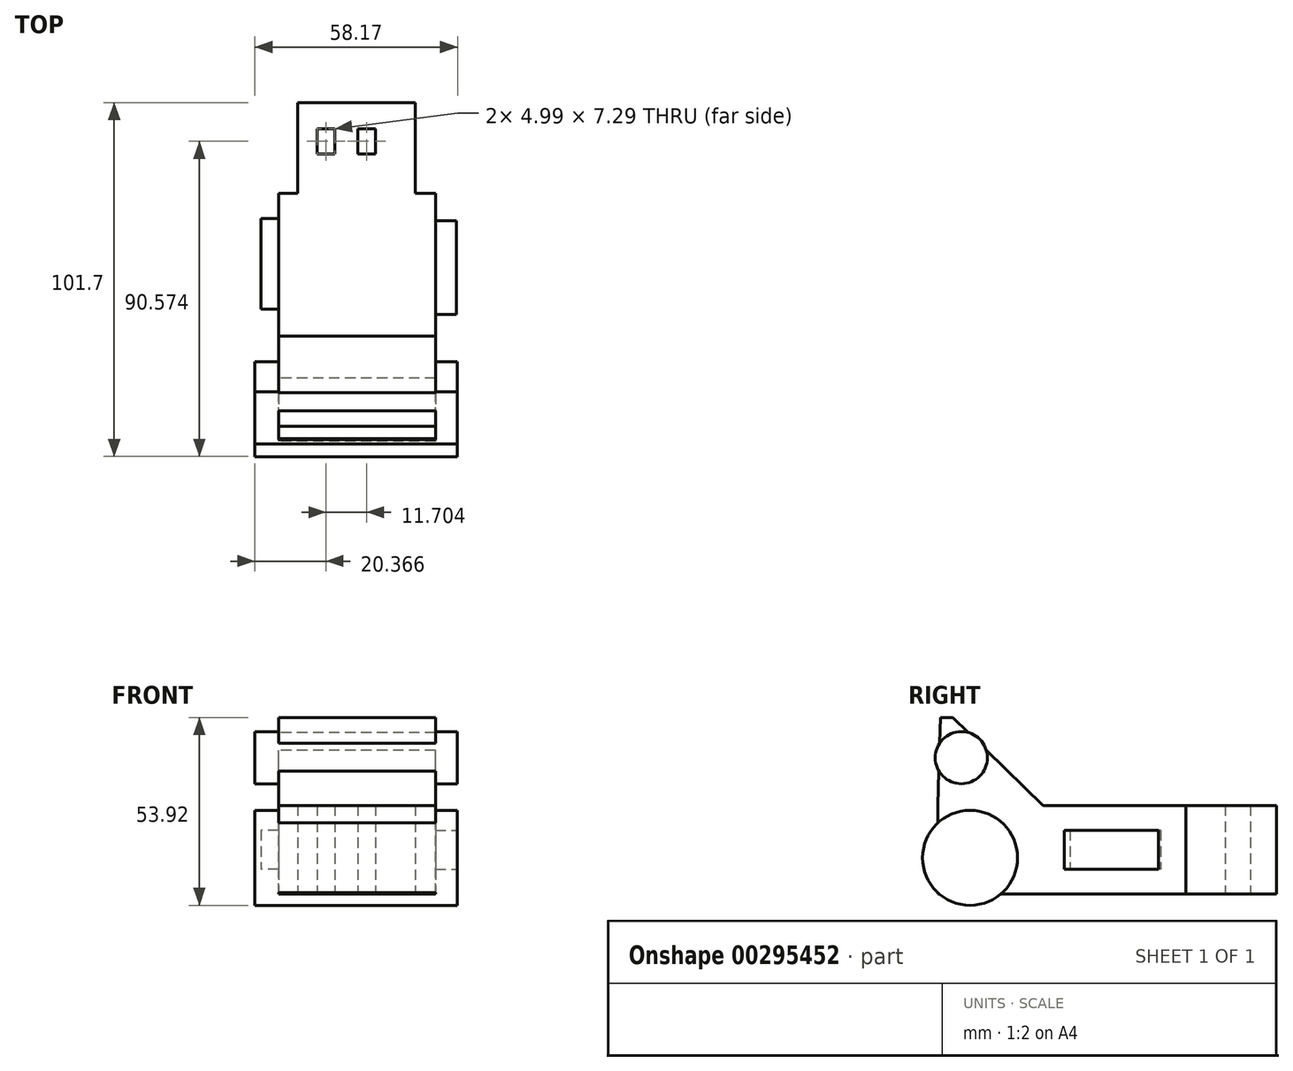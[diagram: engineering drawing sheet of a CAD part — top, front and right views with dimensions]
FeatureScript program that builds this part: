
annotation { "Feature Type Name" : "Feature", "Feature Type Description" : "" }
export const myFeature = defineFeature(function(context is Context, id is Id, definition is map)
    precondition{}
    {
        {
            var Q0;
            Q0=qCreatedBy(makeId("Top.planeOp"),FACE);
            var sketch = newSketch(context, id + "F0", { "sketchPlane" : qUnion([Q0])});
            skLineSegment(sketch, "E0.bottom", {"start": v(-10.55, 40.3) * mm, "end": v(23.22, 40.3) * mm});
            skLineSegment(sketch, "E0.top", {"start": v(-10.55, 14.2) * mm, "end": v(23.22, 14.2) * mm});
            skLineSegment(sketch, "E0.left", {"start": v(-10.55, 40.3) * mm, "end": v(-10.55, 14.2) * mm});
            skLineSegment(sketch, "E0.right", {"start": v(23.22, 40.3) * mm, "end": v(23.22, 14.2) * mm});
            skLineSegment(sketch, "E1.bottom", {"start": v(-16.12, 14.2) * mm, "end": v(28.97, 14.2) * mm});
            skLineSegment(sketch, "E1.top", {"start": v(-16.12, -28.01) * mm, "end": v(28.97, -28.01) * mm});
            skLineSegment(sketch, "E1.left", {"start": v(-16.12, 14.2) * mm, "end": v(-16.12, -28.01) * mm});
            skLineSegment(sketch, "E1.right", {"start": v(28.97, 14.2) * mm, "end": v(28.97, -28.01) * mm});
            skLineSegment(sketch, "E2.top", {"start": v(-16.12, -56.99) * mm, "end": v(28.97, -56.99) * mm});
            skLineSegment(sketch, "E2.left", {"start": v(-16.12, -28.01) * mm, "end": v(-16.12, -56.99) * mm});
            skLineSegment(sketch, "E2.right", {"start": v(28.97, -28.01) * mm, "end": v(28.97, -56.99) * mm});
            skLineSegment(sketch, "E3.bottom", {"start": v(-4.99, 32.8) * mm, "end": v(0, 32.8) * mm});
            skLineSegment(sketch, "E3.top", {"start": v(-4.99, 25.52) * mm, "end": v(0, 25.52) * mm});
            skLineSegment(sketch, "E3.left", {"start": v(-4.99, 32.8) * mm, "end": v(-4.99, 25.52) * mm});
            skLineSegment(sketch, "E3.right", {"start": v(0, 32.8) * mm, "end": v(0, 25.52) * mm});
            skLineSegment(sketch, "E4.bottom", {"start": v(6.72, 32.8) * mm, "end": v(11.7, 32.8) * mm});
            skLineSegment(sketch, "E4.top", {"start": v(6.72, 25.52) * mm, "end": v(11.7, 25.52) * mm});
            skLineSegment(sketch, "E4.left", {"start": v(6.72, 32.8) * mm, "end": v(6.72, 25.52) * mm});
            skLineSegment(sketch, "E4.right", {"start": v(11.7, 32.8) * mm, "end": v(11.7, 25.52) * mm});
            skLineSegment(sketch, "E5.bottom", {"start": v(6.72, 32.8) * mm, "end": v(6.72, 32.8) * mm});
            skPoint(sketch, "E5.top.end.orphan", {"position": v(6.72, 33.77) * mm});
            skSolve(sketch);
        }
        {
            var Q0;
            Q0 = qSketchRegion(id + "F0", true);
            extrude(context, id + "F1", {"entities" : qUnion([Q0]), "depth" : 25.4 * mm});
        }
        {
            var Q0;
            Q0=makeQuery(id+"F1.opExtrude","SWEPT_FACE",FACE,{"disambiguationData":[OSD([sQuery(id+"F0.wireOp",EDGE,"E1.left"),sQuery(id+"F0.wireOp",EDGE,"E2.left")])]});
            var sketch = newSketch(context, id + "F2", { "sketchPlane" : qUnion([Q0])});
            skLineSegment(sketch, "E6", {"start": v(26.78, 25.4) * mm, "end": v(56.22, 54.1) * mm});
            skLineSegment(sketch, "E7", {"start": v(56.22, 54.1) * mm, "end": v(56.99, 25.4) * mm});
            skLineSegment(sketch, "E8", {"start": v(26.78, 25.4) * mm, "end": v(56.99, 25.4) * mm});
            skSolve(sketch);
        }
        {
            var Q0;
            Q0 = qSketchRegion(id + "F2", true);
            var Q1;
            Q1=makeQuery(id+"F1.opExtrude","SWEPT_FACE",FACE,{"disambiguationData":[OSD([sQuery(id+"F0.wireOp",EDGE,"E1.right"),sQuery(id+"F0.wireOp",EDGE,"E2.right")])]});
            extrude(context, id + "F3", {"entities" : qUnion([Q0]), "operationType" : NewBodyOperationType.ADD, "endBound" : BoundingType.UP_TO_SURFACE, "oppositeDirection" : true, "endBoundEntityFace" : qUnion([Q1]), "depth" : 45.2 * mm});
        }
        {
            var Q0;
            Q0=qCreatedBy(makeId("Right.planeOp"),FACE);
            var sketch = newSketch(context, id + "F4", { "sketchPlane" : qUnion([Q0])});
            skCircle(sketch, "E9", {"center": v(-50.27, 39.14) * mm, "radius": 7.5 * mm});
            skCircle(sketch, "E10", {"center": v(-47.78, 10.36) * mm, "radius": 13.63 * mm});
            skSolve(sketch);
        }
        {
            var Q0;
            Q0 = qSketchRegion(id + "F4", true);
            extrude(context, id + "F5", {"entities" : qUnion([Q0]), "operationType" : NewBodyOperationType.ADD, "depth" : 35.3 * mm, "hasSecondDirection" : true, "secondDirectionOppositeDirection" : true, "secondDirectionDepth" : 22.86 * mm});
        }
        {
            var Q0;
            Q0 = qSketchRegion(id + "F0", true);
            extrude(context, id + "F6", {"entities" : qUnion([Q0]), "operationType" : NewBodyOperationType.ADD, "depth" : 25.4 * mm});
        }
        {
            var Q0;
            Q0=qCreatedBy(makeId("Right.planeOp"),FACE);
            var sketch = newSketch(context, id + "F7", { "sketchPlane" : qUnion([Q0])});
            skLineSegment(sketch, "E11", {"start": v(-56.4, 50.65) * mm, "end": v(-52.38, 50.65) * mm});
            skLineSegment(sketch, "E12", {"start": v(-56.4, 50.65) * mm, "end": v(-56.4, 54.5) * mm});
            skLineSegment(sketch, "E13", {"start": v(-56.4, 54.5) * mm, "end": v(-52.38, 50.65) * mm});
            skSolve(sketch);
        }
        {
            var Q0;
            Q0 = qSketchRegion(id + "F7", true);
            extrude(context, id + "F8", {"entities" : qUnion([Q0]), "operationType" : NewBodyOperationType.REMOVE, "endBound" : BoundingType.THROUGH_ALL, "oppositeDirection" : true, "depth" : 25.4 * mm, "hasSecondDirection" : true, "secondDirectionBound" : SecondDirectionBoundingType.THROUGH_ALL, "secondDirectionOppositeDirection" : false, "secondDirectionDepth" : 25.4 * mm});
        }
        {
            var Q0;
            Q0=makeQuery(id+"F1.opExtrude","SWEPT_EDGE",EDGE,{"disambiguationData":[OSD([sQuery(id+"F0.wireOp",EDGE,"E1.bottom"),sQuery(id+"F0.wireOp",EDGE,"E1.left")])]});
            cPoint(context, id + "F9", {"entities" : qUnion([Q0]), "parameter" : 0.5});
        }
        {
            var Q0;
            Q0=qCreatedBy(makeId("Top.planeOp"),FACE);
            var Q1;
            Q1 = qCreatedBy(id + "F9" ,VERTEX);
            cPlane(context, id + "F10", {"entities" : qUnion([Q0, Q1]), "cplaneType" : CPlaneType.PLANE_POINT, "offset" : 25.4 * mm, "width" : 152.4 * mm, "height" : 152.4 * mm});
        }
        {
            var Q0;
            Q0=qCreatedBy(id+"F10.planeOp",FACE);
            var sketch = newSketch(context, id + "F11", { "sketchPlane" : qUnion([Q0])});
            skLineSegment(sketch, "E14.bottom", {"start": v(-16.12, 7.02) * mm, "end": v(-21.1, 7.02) * mm});
            skLineSegment(sketch, "E14.top", {"start": v(-16.12, -19.09) * mm, "end": v(-21.1, -19.09) * mm});
            skLineSegment(sketch, "E14.left", {"start": v(-16.12, 7.02) * mm, "end": v(-16.12, -19.09) * mm});
            skLineSegment(sketch, "E14.right", {"start": v(-21.1, 7.02) * mm, "end": v(-21.1, -19.09) * mm});
            skLineSegment(sketch, "E15", {"start": v(28.97, -20.64) * mm, "end": v(28.97, -20.64) * mm});
            skLineSegment(sketch, "E16.bottom", {"start": v(28.97, 6.33) * mm, "end": v(34.98, 6.33) * mm});
            skLineSegment(sketch, "E16.top", {"start": v(28.97, -20.64) * mm, "end": v(34.98, -20.64) * mm});
            skLineSegment(sketch, "E16.left", {"start": v(28.97, 6.33) * mm, "end": v(28.97, -20.64) * mm});
            skLineSegment(sketch, "E16.right", {"start": v(34.98, 6.33) * mm, "end": v(34.98, -20.64) * mm});
            skSolve(sketch);
        }
        {
            var Q0;
            Q0=makeQuery(id+"F11.imprint","IMPRINT",FACE,{"disambiguationData":[TD([[makeQuery(id+"F11.imprint","IMPRINT",EDGE,{"derivedFrom":sQuery(id+"F11.wireOp",EDGE,"E14.bottom")}),1.0]])]});
            var Q1;
            Q1=makeQuery(id+"F11.imprint","IMPRINT",FACE,{"disambiguationData":[TD([[makeQuery(id+"F11.imprint","IMPRINT",EDGE,{"derivedFrom":sQuery(id+"F11.wireOp",EDGE,"E16.bottom")}),-1.0]])]});
            var Q2;
            Q2 = qConstructionFilter(qBodyType(qCreatedBy(id + "F11" ,EDGE), BodyType.WIRE), ConstructionObject.NO);
            extrude(context, id + "F12", {"entities" : qUnion([Q0, Q1]), "operationType" : NewBodyOperationType.ADD, "surfaceEntities" : qUnion([Q2]), "endBound" : BoundingType.SYMMETRIC, "depth" : 11.18 * mm});
        }
    });
